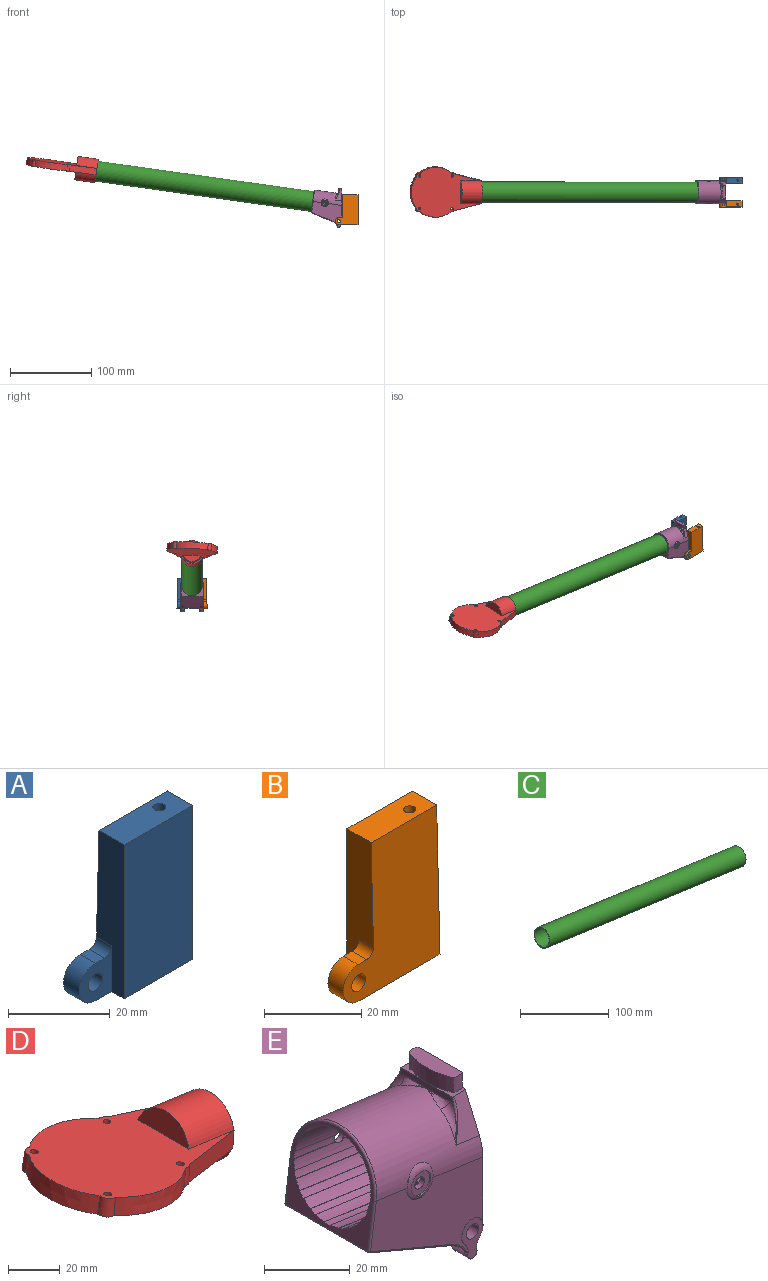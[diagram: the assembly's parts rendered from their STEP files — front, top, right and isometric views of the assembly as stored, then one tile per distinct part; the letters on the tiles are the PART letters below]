
ASSEMBLY  parts=5 mates=3
PART A: 15 faces, bbox 28x8x37 mm
  f0: cylinder r=2mm len=4.43mm, axis (0,-1,0), area 55mm2, adj f3,f9
  f1: plane 37x19mm, normal (0,-1,0), area 703mm2, adj f4,f5,f6,f8
  f2: cylinder r=4.5mm len=9mm, axis (0,-1,0), area 61.9mm2, adj f3,f7,f8,f9
  f3: plane 37x28mm, normal (0,1,0.03), area 763.9mm2, adj f0,f2,f4,f5,f6,f7,f8,f10
  f4: plane 37x8mm, normal (1,0,0), area 277.5mm2, adj f1,f3,f5,f8
  f5: plane 19x7mm, normal (0,0,1), area 128.1mm2, adj f1,f3,f4,f6,f14
  f6: plane 37x7.7mm, normal (-1,0,0), area 229.6mm2, adj f1,f3,f5,f8,f9,f10
  f7: plane 4.26x2.5mm, normal (0,0,1), area 10.6mm2, adj f2,f3,f9,f10
  f8: plane 23.5x8mm, normal (0,0,-1), area 167.3mm2, adj f1,f2,f3,f4,f6,f9,f12
  f9: plane 11x9mm, normal (0,-1,0), area 60.6mm2, adj f0,f2,f6,f7,f8,f10
  f10: cylinder r=2mm len=4.26mm, axis (0,1,0), area 13.3mm2, adj f3,f6,f7,f9
  f11: cone r=0mm half-angle=59deg, axis (0,0,-1), area 5.7mm2, adj f12
  f12: cylinder r=1.25mm len=13.5mm, axis (0,0,-1), area 106mm2, adj f8,f11
  f13: cone r=0mm half-angle=59deg, axis (0,0,1), area 5.7mm2, adj f14
  f14: cylinder r=1.25mm len=13.5mm, axis (0,0,1), area 106mm2, adj f5,f13
PART B: 15 faces, bbox 28x8x37 mm
  f0: cylinder r=2mm len=4.43mm, axis (0,1,0), area 55mm2, adj f3,f9
  f1: plane 37x19mm, normal (0,1,0), area 703mm2, adj f4,f5,f6,f8
  f2: cylinder r=4.5mm len=9mm, axis (0,1,0), area 61.9mm2, adj f3,f7,f8,f9
  f3: plane 37x28mm, normal (0,-1,0.03), area 763.9mm2, adj f0,f2,f4,f5,f6,f7,f8,f10
  f4: plane 37x8mm, normal (1,0,0), area 277.5mm2, adj f1,f3,f5,f8
  f5: plane 19x7mm, normal (0,0,1), area 128.1mm2, adj f1,f3,f4,f6,f14
  f6: plane 37x7.7mm, normal (-1,0,0), area 229.6mm2, adj f1,f3,f5,f8,f9,f10
  f7: plane 4.26x2.5mm, normal (0,0,1), area 10.6mm2, adj f2,f3,f9,f10
  f8: plane 23.5x8mm, normal (0,0,-1), area 167.3mm2, adj f1,f2,f3,f4,f6,f9,f12
  f9: plane 11x9mm, normal (0,1,0), area 60.6mm2, adj f0,f2,f6,f7,f8,f10
  f10: cylinder r=2mm len=4.26mm, axis (0,-1,0), area 13.3mm2, adj f3,f6,f7,f9
  f11: cone r=0mm half-angle=59deg, axis (0,0,-1), area 5.7mm2, adj f12
  f12: cylinder r=1.25mm len=13.5mm, axis (0,0,-1), area 106mm2, adj f8,f11
  f13: cone r=0mm half-angle=59deg, axis (0,0,1), area 5.7mm2, adj f14
  f14: cylinder r=1.25mm len=13.5mm, axis (0,0,1), area 106mm2, adj f5,f13
PART C: 4 faces, bbox 316.9x25x68.8 mm
  f0: cylinder r=12.5mm len=316.9mm, axis (0.99,0,-0.14), area 24857.9mm2, adj f1,f3
  f1: plane 25x24.76mm, normal (0.99,0,-0.14), area 75.4mm2, adj f0,f2
  f2: cylinder r=11.5mm len=316.62mm, axis (0.99,0,-0.14), area 22869.2mm2, adj f1,f3
  f3: plane 25x24.76mm, normal (-0.99,0,0.14), area 75.4mm2, adj f0,f2
PART D: 22 faces, bbox 88.7x62x32.2 mm
  f0: plane 85.74x61.16mm, normal (0.14,0,0.99), area 3234.5mm2, adj f2,f3,f4,f5,f6,f7,f8,f9
  f1: plane 86.15x62mm, normal (-0.14,0,-0.99), area 3325.5mm2, adj f2,f3,f4,f5,f6,f7,f8,f9
  f2: cone r=4mm half-angle=3deg, axis (-0.14,0,-0.99), area 59.2mm2, adj f0,f1,f3,f14
  f3: cone r=31mm half-angle=3deg, axis (-0.14,0,-0.99), area 337.2mm2, adj f0,f1,f2,f4
  f4: cone r=4mm half-angle=3deg, axis (-0.14,0,-0.99), area 59.2mm2, adj f0,f1,f3,f5
  f5: cone r=31mm half-angle=3deg, axis (-0.14,0,-0.99), area 337.2mm2, adj f0,f1,f4,f6
  f6: cone r=4mm half-angle=3deg, axis (-0.14,0,-0.99), area 30.1mm2, adj f0,f1,f5,f7
  f7: plane 33.82x12.55mm, normal (0.25,-0.97,0.02), area 274mm2, adj f0,f1,f6,f8
  f8: plane 29x28.72mm, normal (0.99,0,-0.14), area 169.2mm2, adj f0,f1,f7,f9,f16,f19,f21
  f9: plane 33.82x12.55mm, normal (0.25,0.97,0.02), area 274mm2, adj f0,f1,f8,f10
  f10: cone r=4mm half-angle=3deg, axis (-0.14,0,-0.99), area 30.1mm2, adj f0,f1,f9,f14
  f11: cylinder r=1.5mm len=8.34mm, axis (-0.14,0,-0.99), area 75.4mm2, adj f0,f1
  f12: cylinder r=1.5mm len=8.34mm, axis (-0.14,0,-0.99), area 75.4mm2, adj f0,f1
  f13: cylinder r=1.5mm len=8.34mm, axis (-0.14,0,-0.99), area 75.4mm2, adj f0,f1
  f14: cone r=31mm half-angle=3deg, axis (-0.14,0,-0.99), area 337.2mm2, adj f0,f1,f2,f10
  f15: cylinder r=1.5mm len=8.34mm, axis (-0.14,0,-0.99), area 75.4mm2, adj f0,f1
  f16: cylinder r=14.5mm len=27.87mm, axis (-0.99,0,0.14), area 936.2mm2, adj f1,f8,f17
  f17: plane 27.87x10.4mm, normal (-0.99,0,0.14), area 215.7mm2, adj f1,f16
  f18: plane 27.87x10.4mm, normal (-0.99,0,0.14), area 215.7mm2, adj f0,f19
  f19: cylinder r=14.5mm len=27.87mm, axis (-0.99,0,0.14), area 936.2mm2, adj f0,f8,f18
  f20: plane 25x24.76mm, normal (0.99,0,-0.14), area 490.9mm2, adj f21
  f21: cylinder r=12.5mm len=28.03mm, axis (0.99,0,-0.14), area 1845.7mm2, adj f8,f20
PART E: 138 faces, bbox 40.7x34.8x48 mm
  f0: cylinder r=10mm len=5.84mm, axis (0,1,0), area 37.2mm2, adj f1,f36,f119,f130
  f1: cylinder r=1.5mm len=5.1mm, axis (0,1,0), area 23.1mm2, adj f0,f2,f40,f41,f119,f130
  f2: cylinder r=4mm len=5.1mm, axis (0,1,0), area 19.4mm2, adj f1,f35,f41,f119
  f3: plane 13.62x1.92mm, normal (0.14,-0.08,0.99), area 1.4mm2, adj f21,f54,f68,f116
  f4: cylinder r=12.6mm len=13.9mm, axis (-0.99,0,0.14), area 27.5mm2, adj f27,f67,f69,f116
  f5: plane 13.62x1.92mm, normal (-0.14,-0.08,-0.99), area 1.4mm2, adj f22,f54,f68,f116
  f6: plane 13.62x1.92mm, normal (-0.14,0.08,-0.99), area 1.4mm2, adj f7,f13,f27,f117
  f7: cylinder r=12.6mm len=13.9mm, axis (-0.99,0,0.14), area 27.5mm2, adj f6,f8,f27,f117
  f8: plane 13.62x1.92mm, normal (0.14,0.08,0.99), area 1.4mm2, adj f7,f14,f27,f117
  f9: cylinder r=14mm len=37.01mm, axis (-0.99,0,0.14), area 1218.4mm2, adj f28,f29,f30,f52,f53,f109,f110,f114
  f10: cylinder r=12.5mm len=29.79mm, axis (-0.99,0,0.14), area 87.7mm2, adj f27,f54,f57,f100
  f11: cylinder r=12.5mm len=29.93mm, axis (-0.99,0,0.14), area 87.7mm2, adj f27,f54,f97,f102
  f12: cylinder r=12.5mm len=30.05mm, axis (-0.99,0,0.14), area 87.7mm2, adj f27,f54,f94,f99
  f13: cylinder r=12.5mm len=30.11mm, axis (-0.99,0,0.14), area 86.7mm2, adj f6,f27,f54,f91,f96,f117
  f14: cylinder r=12.5mm len=30.11mm, axis (-0.99,0,0.14), area 86.6mm2, adj f8,f27,f54,f88,f93,f117
  f15: cylinder r=12.5mm len=30.05mm, axis (-0.99,0,0.14), area 87.7mm2, adj f27,f54,f85,f90
  f16: cylinder r=12.5mm len=29.93mm, axis (-0.99,0,0.14), area 87.7mm2, adj f27,f54,f82,f87
  f17: cylinder r=12.5mm len=29.79mm, axis (-0.99,0,0.14), area 87.7mm2, adj f27,f54,f79,f84
  f18: cylinder r=12.5mm len=29.79mm, axis (-0.99,0,0.14), area 87.7mm2, adj f27,f54,f76,f81
  f19: cylinder r=12.5mm len=29.93mm, axis (-0.99,0,0.14), area 87.7mm2, adj f27,f54,f73,f78
  f20: cylinder r=12.5mm len=30.05mm, axis (-0.99,0,0.14), area 87.7mm2, adj f27,f54,f70,f75
  f21: cylinder r=12.5mm len=30.11mm, axis (-0.99,0,0.14), area 86.6mm2, adj f3,f27,f54,f67,f72,f116
  f22: cylinder r=12.5mm len=30.11mm, axis (-0.99,0,0.14), area 86.7mm2, adj f5,f27,f54,f64,f69,f116
  f23: cylinder r=12.5mm len=30.05mm, axis (-0.99,0,0.14), area 87.7mm2, adj f27,f54,f61,f66
  f24: cylinder r=12.5mm len=29.93mm, axis (-0.99,0,0.14), area 87.7mm2, adj f27,f54,f58,f63
  f25: cylinder r=12.5mm len=29.79mm, axis (-0.99,0,0.14), area 87.7mm2, adj f27,f54,f55,f60
  f26: cylinder r=12.5mm len=25.51mm, axis (-0.99,0,0.14), area 279mm2, adj f106,f137
  f27: plane 27x26.85mm, normal (-0.99,0,0.14), area 159.8mm2, adj f4,f6,f7,f8,f10,f11,f12,f13
  f28: plane 36.95x29.79mm, normal (0,1,0), area 620.1mm2, adj f9,f30,f35,f40,f109,f130,f133,f136
  f29: plane 36.95x29.79mm, normal (0,-1,0), area 620.1mm2, adj f9,f30,f35,f43,f115,f127,f128,f131
  f30: plane 40.17x28.02mm, normal (1,0,0), area 451.6mm2, adj f9,f28,f29,f31,f34,f35,f45,f49
  f31: plane 8.53x4.52mm, normal (0,0,1), area 7.9mm2, adj f30,f32,f48,f49,f53,f125
  f32: plane 17.95x1.83mm, normal (-1,0,0), area 29.3mm2, adj f31,f33,f34,f51,f122,f123,f125,f126
  f33: plane 1.3x0.8mm, normal (-0.99,0,0.14), area 0.4mm2, adj f32,f124,f125
  f34: plane 8.53x4.52mm, normal (0,0,1), area 7.8mm2, adj f30,f32,f45,f46,f47,f48,f52,f126
  f35: cylinder r=3.5mm len=28.2mm, axis (0,1,0), area 179.8mm2, adj f2,f28,f29,f30,f39,f40,f41,f43
  f36: plane 31.51x27mm, normal (-0.39,0,-0.92), area 876.8mm2, adj f0,f37,f118,f119,f120,f128,f132,f133
  f37: cylinder r=10mm len=5.84mm, axis (0,1,0), area 37.2mm2, adj f36,f38,f120,f127
  f38: cylinder r=1.5mm len=5.1mm, axis (0,1,0), area 23.1mm2, adj f37,f39,f43,f44,f120,f127
  f39: cylinder r=4mm len=5.1mm, axis (0,1,0), area 19.4mm2, adj f35,f38,f44,f120
  f40: cylinder r=4mm len=3.5mm, axis (0,1,0), area 0.4mm2, adj f1,f28,f35,f41,f130
  f41: plane 11.2x7mm, normal (0,1,0), area 38.3mm2, adj f1,f2,f35,f40,f42
  f42: cylinder r=2mm len=28.2mm, axis (0,1,0), area 354.4mm2, adj f41,f44
  f43: cylinder r=4mm len=3.5mm, axis (0,1,0), area 0.4mm2, adj f29,f35,f38,f44,f127
  f44: plane 11.2x7mm, normal (0,-1,0), area 38.3mm2, adj f35,f38,f39,f42,f43
  f45: cylinder r=3.19mm len=4.25mm, axis (0,0,-1), area 13.3mm2, adj f30,f34,f46,f50
  f46: cylinder r=18.27mm len=4.25mm, axis (0,0,-1), area 1mm2, adj f34,f45,f47,f50
  f47: cylinder r=0.45mm len=4.25mm, axis (0,0,-1), area 4.2mm2, adj f34,f46,f48,f50
  f48: cylinder r=18.27mm len=13.53mm, axis (0,0,-1), area 58.9mm2, adj f31,f34,f47,f49,f50
  f49: cylinder r=3.19mm len=4.25mm, axis (0,0,-1), area 13.3mm2, adj f30,f31,f48,f50
  f50: plane 15.25x4.5mm, normal (0,0,1), area 59.8mm2, adj f30,f45,f46,f47,f48,f49
  f51: plane 1.3x0.8mm, normal (-0.99,0,0.14), area 0.4mm2, adj f32,f121,f126
  f52: plane 10.9x7.66mm, normal (0.05,0.92,0.39), area 60.1mm2, adj f9,f30,f34,f126
  f53: plane 10.9x7.66mm, normal (0.05,-0.92,0.39), area 60.1mm2, adj f9,f30,f31,f125
  f54: plane 25.2x24.95mm, normal (-0.99,0,0.14), area 78.6mm2, adj f3,f5,f10,f11,f12,f13,f14,f15
  f55: plane 29.72x4.27mm, normal (0.01,1,0.08), area 3mm2, adj f25,f27,f54,f56
  f56: cylinder r=12.6mm len=29.71mm, axis (-0.99,0,0.14), area 60.1mm2, adj f27,f54,f55,f57
  f57: plane 29.72x4.27mm, normal (0.01,-1,0.08), area 3mm2, adj f10,f27,f54,f56
  f58: plane 29.72x4.26mm, normal (0.06,0.89,0.45), area 3mm2, adj f24,f27,f54,f59
  f59: cylinder r=12.6mm len=29.81mm, axis (-0.99,0,0.14), area 60.1mm2, adj f27,f54,f58,f60
  f60: plane 29.72x4.27mm, normal (-0.04,-0.95,-0.31), area 3mm2, adj f25,f27,f54,f59
  f61: plane 29.72x4.24mm, normal (0.11,0.65,0.75), area 3mm2, adj f23,f27,f54,f62
  f62: cylinder r=12.6mm len=29.91mm, axis (-0.99,0,0.14), area 60.1mm2, adj f27,f54,f61,f63
  f63: plane 29.72x4.25mm, normal (-0.09,-0.76,-0.64), area 3mm2, adj f24,f27,f54,f62
  f64: plane 29.71x4.21mm, normal (0.13,0.31,0.94), area 3mm2, adj f22,f27,f54,f65
  f65: cylinder r=12.6mm len=29.97mm, axis (-0.99,0,0.14), area 60.1mm2, adj f27,f54,f64,f66
  f66: plane 29.71x4.22mm, normal (-0.12,-0.45,-0.88), area 3mm2, adj f23,f27,f54,f65
  f67: plane 13.62x1.92mm, normal (0.14,-0.08,0.99), area 1.4mm2, adj f4,f21,f27,f116
  f68: cylinder r=12.6mm len=13.9mm, axis (-0.99,0,0.14), area 27.5mm2, adj f3,f5,f54,f116
  f69: plane 13.62x1.92mm, normal (-0.14,-0.08,-0.99), area 1.4mm2, adj f4,f22,f27,f116
  f70: plane 29.71x4.22mm, normal (0.12,-0.45,0.88), area 3mm2, adj f20,f27,f54,f71
  f71: cylinder r=12.6mm len=29.97mm, axis (-0.99,0,0.14), area 60.1mm2, adj f27,f54,f70,f72
  f72: plane 29.71x4.21mm, normal (-0.13,0.31,-0.94), area 3mm2, adj f21,f27,f54,f71
  f73: plane 29.72x4.25mm, normal (0.09,-0.76,0.64), area 3mm2, adj f19,f27,f54,f74
  f74: cylinder r=12.6mm len=29.91mm, axis (-0.99,0,0.14), area 60.1mm2, adj f27,f54,f73,f75
  f75: plane 29.72x4.24mm, normal (-0.11,0.65,-0.75), area 3mm2, adj f20,f27,f54,f74
  f76: plane 29.72x4.27mm, normal (0.04,-0.95,0.31), area 3mm2, adj f18,f27,f54,f77
  f77: cylinder r=12.6mm len=29.81mm, axis (-0.99,0,0.14), area 60.1mm2, adj f27,f54,f76,f78
  f78: plane 29.72x4.26mm, normal (-0.06,0.89,-0.45), area 3mm2, adj f19,f27,f54,f77
  f79: plane 29.72x4.27mm, normal (-0.01,-1,-0.08), area 3mm2, adj f17,f27,f54,f80
  f80: cylinder r=12.6mm len=29.71mm, axis (-0.99,0,0.14), area 60.1mm2, adj f27,f54,f79,f81
  f81: plane 29.72x4.27mm, normal (-0.01,1,-0.08), area 3mm2, adj f18,f27,f54,f80
  f82: plane 29.72x4.26mm, normal (-0.06,-0.89,-0.45), area 3mm2, adj f16,f27,f54,f83
  f83: cylinder r=12.6mm len=29.81mm, axis (-0.99,0,0.14), area 60.1mm2, adj f27,f54,f82,f84
  f84: plane 29.72x4.27mm, normal (0.04,0.95,0.31), area 3mm2, adj f17,f27,f54,f83
  f85: plane 29.72x4.24mm, normal (-0.11,-0.65,-0.75), area 3mm2, adj f15,f27,f54,f86
  f86: cylinder r=12.6mm len=29.91mm, axis (-0.99,0,0.14), area 60.1mm2, adj f27,f54,f85,f87
  f87: plane 29.72x4.25mm, normal (0.09,0.76,0.64), area 3mm2, adj f16,f27,f54,f86
  f88: plane 29.71x4.21mm, normal (-0.13,-0.31,-0.94), area 3mm2, adj f14,f27,f54,f89
  f89: cylinder r=12.6mm len=29.97mm, axis (-0.99,0,0.14), area 60.1mm2, adj f27,f54,f88,f90
  f90: plane 29.71x4.22mm, normal (0.12,0.45,0.88), area 3mm2, adj f15,f27,f54,f89
  f91: plane 13.62x1.92mm, normal (-0.14,0.08,-0.99), area 1.4mm2, adj f13,f54,f92,f117
  f92: cylinder r=12.6mm len=13.9mm, axis (-0.99,0,0.14), area 27.5mm2, adj f54,f91,f93,f117
  f93: plane 13.62x1.92mm, normal (0.14,0.08,0.99), area 1.4mm2, adj f14,f54,f92,f117
  f94: plane 29.71x4.22mm, normal (-0.12,0.45,-0.88), area 3mm2, adj f12,f27,f54,f95
  f95: cylinder r=12.6mm len=29.97mm, axis (-0.99,0,0.14), area 60.1mm2, adj f27,f54,f94,f96
  f96: plane 29.71x4.21mm, normal (0.13,-0.31,0.94), area 3mm2, adj f13,f27,f54,f95
  f97: plane 29.72x4.25mm, normal (-0.09,0.76,-0.64), area 3mm2, adj f11,f27,f54,f98
  f98: cylinder r=12.6mm len=29.91mm, axis (-0.99,0,0.14), area 60.1mm2, adj f27,f54,f97,f99
  f99: plane 29.72x4.24mm, normal (0.11,-0.65,0.75), area 3mm2, adj f12,f27,f54,f98
  f100: plane 29.72x4.27mm, normal (-0.04,0.95,-0.31), area 3mm2, adj f10,f27,f54,f101
  f101: cylinder r=12.6mm len=29.81mm, axis (-0.99,0,0.14), area 60.1mm2, adj f27,f54,f100,f102
  f102: plane 29.72x4.26mm, normal (0.06,-0.89,0.45), area 3mm2, adj f11,f27,f54,f101
  f103: cylinder r=11.5mm len=23mm, axis (-0.99,0,0.14), area 108.4mm2, adj f54,f107
  f104: plane 22x21.79mm, normal (-0.99,0,0.14), area 66mm2, adj f105,f107
  f105: cylinder r=10mm len=20.34mm, axis (-0.99,0,0.14), area 241.5mm2, adj f104,f106
  f106: plane 25x24.76mm, normal (0.99,0,-0.14), area 176.7mm2, adj f26,f105
  f107: cone r=11mm half-angle=45deg, axis (0.99,0,-0.14), area 50mm2, adj f103,f104
  f108: cylinder r=3.25mm len=6.5mm, axis (0,-1,0), area 8.7mm2, adj f109,f111
  f109: torus R=3.25mm, axis (0,-1,0), area 35.6mm2, adj f9,f28,f108,f110
  f110: plane 1.1x0.15mm, normal (0,-1,0), area 0mm2, adj f9,f109
  f111: plane 6.5x6.5mm, normal (0,1,0), area 25.1mm2, adj f108,f117
  f112: cylinder r=3.25mm len=6.5mm, axis (0,-1,0), area 8.7mm2, adj f113,f115
  f113: plane 6.5x6.5mm, normal (0,-1,0), area 25.1mm2, adj f112,f116
  f114: plane 1.1x0.15mm, normal (0,1,0), area 0mm2, adj f9,f115
  f115: torus R=3.25mm, axis (0,-1,0), area 35.6mm2, adj f9,f29,f112,f114
  f116: cylinder r=1.6mm len=3.2mm, axis (0,1,0), area 14.2mm2, adj f3,f4,f5,f21,f22,f67,f68,f69
  f117: cylinder r=1.6mm len=3.2mm, axis (0,1,0), area 14.2mm2, adj f6,f7,f8,f13,f14,f91,f92,f93
  f118: cylinder r=4mm len=18mm, axis (0,-1,0), area 11mm2, adj f35,f36,f119,f120
  f119: plane 9.46x6.83mm, normal (0,-1,0), area 17.1mm2, adj f0,f1,f2,f35,f36,f118
  f120: plane 9.46x6.83mm, normal (0,1,0), area 17.1mm2, adj f35,f36,f37,f38,f39,f118
  f121: torus R=16mm, axis (0.99,0,-0.14), area 17.2mm2, adj f9,f51,f122,f126
  f122: bspline ~7.75x2.22mm, area 7.1mm2, adj f9,f32,f121
  f123: bspline ~7.75x2.22mm, area 7.1mm2, adj f9,f32,f124
  f124: torus R=16mm, axis (0.99,0,-0.14), area 17.2mm2, adj f9,f33,f123,f125
  f125: bspline ~10.1x5.09mm, area 4.8mm2, adj f31,f32,f33,f53,f124
  f126: bspline ~10.1x5.09mm, area 4.8mm2, adj f32,f34,f51,f52,f121
  f127: torus R=10.5mm, axis (0,-1,0), area 6.1mm2, adj f29,f37,f38,f43,f128
  f128: cylinder r=0.5mm len=26.91mm, axis (-0.92,0,0.39), area 22.8mm2, adj f29,f36,f127,f129
  f129: sphere r=0.5mm, area 0.2mm2, adj f128,f131,f132
  f130: torus R=10.5mm, axis (0,-1,0), area 6.1mm2, adj f0,f1,f28,f40,f133
  f131: cylinder r=0.5mm len=13.55mm, axis (0.14,0,0.99), area 10.7mm2, adj f27,f29,f129,f134
  f132: cylinder r=0.5mm len=27mm, axis (0,1,0), area 17.7mm2, adj f27,f36,f129,f135
  f133: cylinder r=0.5mm len=26.91mm, axis (0.92,0,-0.39), area 22.8mm2, adj f28,f36,f130,f135
  f134: torus R=13.5mm, axis (0.99,0,-0.14), area 34.1mm2, adj f9,f27,f131,f136
  f135: sphere r=0.5mm, area 0.2mm2, adj f132,f133,f136
  f136: cylinder r=0.5mm len=13.55mm, axis (-0.14,0,-0.99), area 10.7mm2, adj f27,f28,f134,f135
  f137: bspline ~26.26x26mm, area 62.9mm2, adj f26,f30
PLACE A at identity
PLACE B at identity fixed
PLACE C rot(axis=(0,-1,0),0deg) t=(0,-0.1,0)mm
PLACE D rot(axis=(0.99,0,-0.14),3deg) t=(0,0.93,0.03)mm
PLACE E rot(axis=(0,-1,0),0deg) t=(0,-0.1,0)mm
MATE revolute D.f21 <-> C.f0  axis (0.99,0,-0.14) through (-320.71,-0.1,65)mm
MATE planar B.f8 <-> A.f8  axis (0,0,-1) through (12.67,-14.7,-4.5)mm
MATE revolute E.f42 <-> A.f0  axis (0,1,0) through (0,14,0)mm
